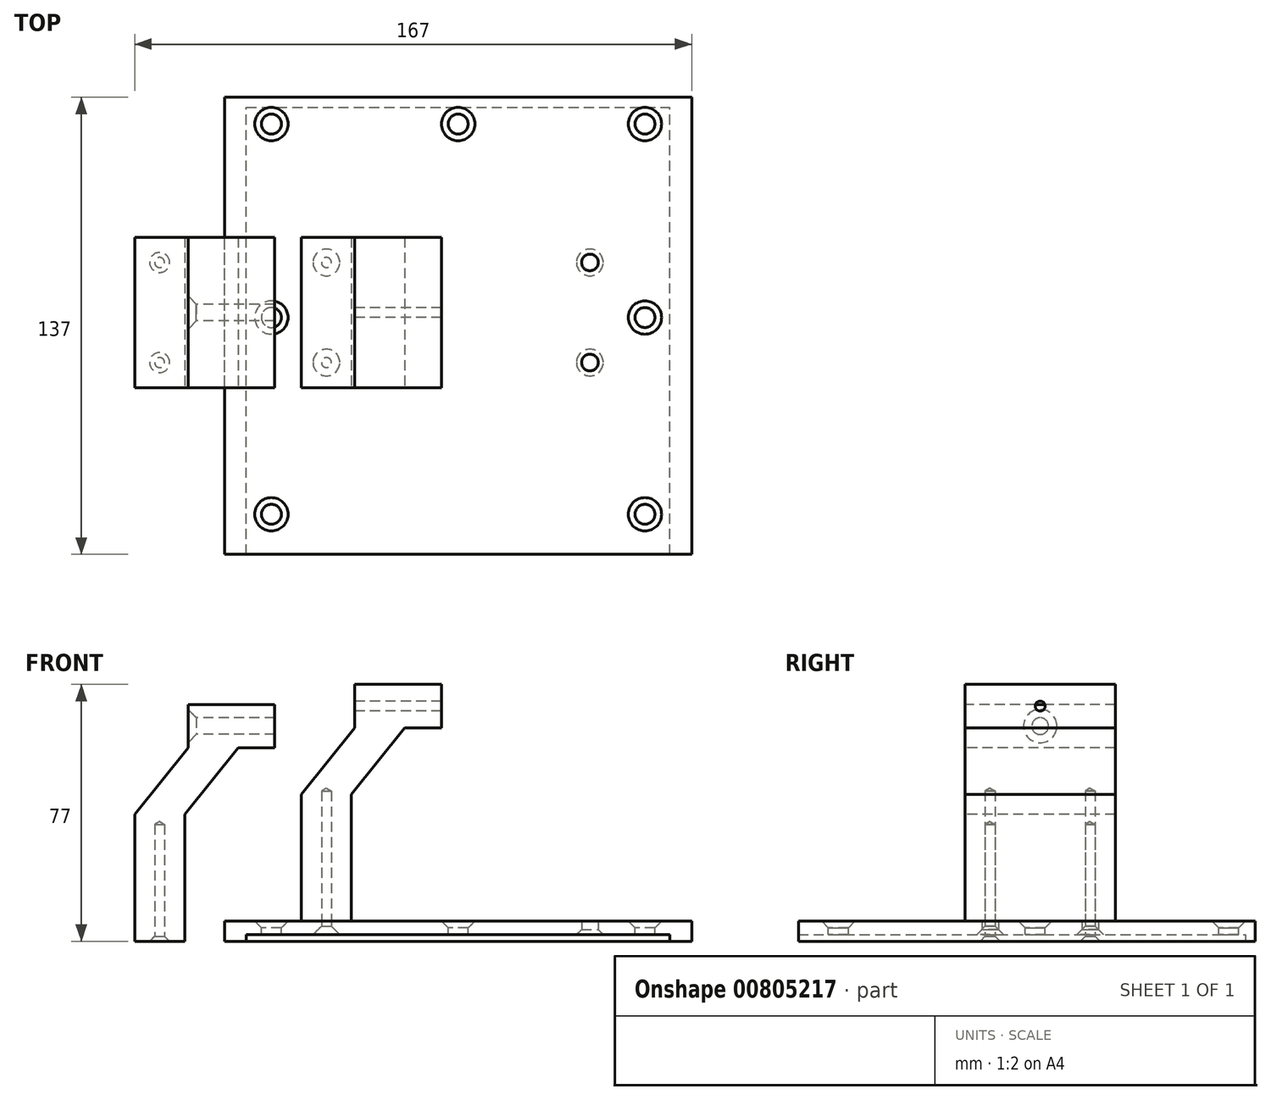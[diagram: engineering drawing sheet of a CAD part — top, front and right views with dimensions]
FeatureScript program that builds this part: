
annotation { "Feature Type Name" : "Feature", "Feature Type Description" : "" }
export const myFeature = defineFeature(function(context is Context, id is Id, definition is map)
    precondition{}
    {
        {
            var Q0;
            Q0=qCreatedBy(makeId("Top.planeOp"),FACE);
            var sketch = newSketch(context, id + "F0", { "sketchPlane" : qUnion([Q0])});
            skLineSegment(sketch, "E0.bottom", {"start": v(0, 0) * mm, "end": v(140, 0) * mm});
            skLineSegment(sketch, "E0.top", {"start": v(0, 137) * mm, "end": v(140, 137) * mm});
            skLineSegment(sketch, "E0.left", {"start": v(0, 0) * mm, "end": v(0, 137) * mm});
            skLineSegment(sketch, "E0.right", {"start": v(140, 0) * mm, "end": v(140, 137) * mm});
            skSolve(sketch);
        }
        {
            var Q0;
            Q0=makeQuery(id+"F0.imprint","IMPRINT",FACE,{"disambiguationData":[TD([[makeQuery(id+"F0.imprint","IMPRINT",EDGE,{"derivedFrom":sQuery(id+"F0.wireOp",EDGE,"E0.bottom")}),1.0]])]});
            extrude(context, id + "F1", {"entities" : qUnion([Q0]), "depth" : 6 * mm, "offsetDistance" : 25 * mm});
        }
        {
            var Q0;
            Q0=makeQuery(id+"F1.opExtrude","CAP_FACE",FACE,{"disambiguationData":[OSD([sQuery(id+"F0.wireOp",EDGE,"E0.bottom"),sQuery(id+"F0.wireOp",EDGE,"E0.top"),sQuery(id+"F0.wireOp",EDGE,"E0.left"),sQuery(id+"F0.wireOp",EDGE,"E0.right")])],"isStart":false});
            var sketch = newSketch(context, id + "F2", { "sketchPlane" : qUnion([Q0])});
            skLineSegment(sketch, "E1", {"start": v(70, 137) * mm, "end": v(70, 0) * mm, "construction": true});
            skLineSegment(sketch, "E2", {"start": v(0, 129) * mm, "end": v(140, 129) * mm, "construction": true});
            skLineSegment(sketch, "E3", {"start": v(0, 107) * mm, "end": v(140, 107) * mm, "construction": true});
            skPoint(sketch, "E4", {"position": v(14, 129) * mm});
            skPoint(sketch, "E5", {"position": v(70, 129) * mm});
            skPoint(sketch, "E6", {"position": v(126, 129) * mm});
            skPoint(sketch, "E7", {"position": v(18, 107) * mm});
            skPoint(sketch, "E8", {"position": v(122, 107) * mm});
            skLineSegment(sketch, "E9", {"start": v(0, 12) * mm, "end": v(140, 12) * mm, "construction": true});
            skLineSegment(sketch, "E10", {"start": v(0, 71) * mm, "end": v(140, 71) * mm, "construction": true});
            skLineSegment(sketch, "E11", {"start": v(14, 135.44) * mm, "end": v(14, 12) * mm, "construction": true});
            skLineSegment(sketch, "E12", {"start": v(126, 12) * mm, "end": v(126, 129) * mm, "construction": true});
            skPoint(sketch, "E13", {"position": v(14, 12) * mm});
            skPoint(sketch, "E14", {"position": v(126, 12) * mm});
            skPoint(sketch, "E15", {"position": v(126, 71) * mm});
            skPoint(sketch, "E16", {"position": v(14, 71) * mm});
            skSolve(sketch);
        }
        {
            var Q0;
            Q0=sQuery(id+"F2.wireOp",VERTEX,"E4");
            var Q1;
            Q1=sQuery(id+"F2.wireOp",VERTEX,"E5");
            var Q2;
            Q2=sQuery(id+"F2.wireOp",VERTEX,"E6");
            var Q3;
            Q3=sQuery(id+"F2.wireOp",VERTEX,"E16");
            var Q4;
            Q4=sQuery(id+"F2.wireOp",VERTEX,"E15");
            var Q5;
            Q5=sQuery(id+"F2.wireOp",VERTEX,"E14");
            var Q6;
            Q6=sQuery(id+"F2.wireOp",VERTEX,"E13");
            var Q7;
            Q7=makeQuery(id+"F1.opExtrude","SWEPT_BODY",BODY,{"disambiguationData":[OSD([sQuery(id+"F0.wireOp",EDGE,"E0.bottom"),sQuery(id+"F0.wireOp",EDGE,"E0.top"),sQuery(id+"F0.wireOp",EDGE,"E0.left"),sQuery(id+"F0.wireOp",EDGE,"E0.right")])]});
            hole(context, id + "F3", {"style" : HoleStyle.C_SINK, "endStyle" : HoleEndStyle.THROUGH, "holeDiameter" : 6 * mm, "cSinkDiameter" : 10 * mm, "cSinkAngle" : 90 * degree, "majorDiameter" : 5 * mm, "isTappedThrough" : true, "tappedDepth" : 12 * mm, "tapClearance" : 3, "startFromSketch" : true, "locations" : qUnion([Q0, Q1, Q2, Q3, Q4, Q5, Q6]), "scope" : qUnion([Q7])});
        }
        {
            var Q0;
            Q0=makeQuery(id+"FzE8ZDCXC4sYmEn_1.boolean.opBoolean","MERGE",FACE,{"derivedFrom":[makeQuery(id+"F1.opExtrude","SWEPT_FACE",FACE,{"disambiguationData":[OSD([sQuery(id+"F0.wireOp",EDGE,"E0.bottom")])]}),makeQuery(id+"FzE8ZDCXC4sYmEn_1.opExtrude","SWEPT_FACE",FACE,{"disambiguationData":[OSD([sQuery(id+"FCP8l3nhgKFZF62_1.wireOp",EDGE,"6PEErpOA-bjMb-Vwhj-6amR-bHppJGbZV4a9.bottom")])]}),makeQuery(id+"FzE8ZDCXC4sYmEn_1.opExtrude","SWEPT_FACE",FACE,{"disambiguationData":[OSD([sQuery(id+"FCP8l3nhgKFZF62_1.wireOp",EDGE,"gd5vmW88-UjtB-D9mt-sBeu-wjY4mzePWb4o.bottom")])]})]});
            var sketch = newSketch(context, id + "F4", { "sketchPlane" : qUnion([Q0])});
            skLineSegment(sketch, "E17", {"start": v(23, 44) * mm, "end": v(39, 64) * mm});
            skLineSegment(sketch, "E18", {"start": v(39, 64) * mm, "end": v(39, 77) * mm});
            skLineSegment(sketch, "E19", {"start": v(39, 77) * mm, "end": v(54, 77) * mm});
            skLineSegment(sketch, "E20", {"start": v(38, 44) * mm, "end": v(54, 64) * mm});
            skLineSegment(sketch, "E21", {"start": v(54, 64) * mm, "end": v(54, 77) * mm});
            skLineSegment(sketch, "E22", {"start": v(70, 6) * mm, "end": v(70, 104.41) * mm, "construction": true});
            skLineSegment(sketch, "E23", {"start": v(23, 44) * mm, "end": v(38, 44) * mm});
            skLineSegment(sketch, "E24", {"start": v(23, 44) * mm, "end": v(23, 6) * mm});
            skLineSegment(sketch, "E25", {"start": v(38, 44) * mm, "end": v(38, 6) * mm});
            skLineSegment(sketch, "E26", {"start": v(23, 6) * mm, "end": v(38, 6) * mm});
            skLineSegment(sketch, "E27", {"start": v(39, 64) * mm, "end": v(54, 64) * mm});
            skSolve(sketch);
        }
        {
            var Q0;
            Q0=makeQuery(id+"F4.imprint","IMPRINT",FACE,{"disambiguationData":[TD([[makeQuery(id+"F4.imprint","IMPRINT",EDGE,{"derivedFrom":sQuery(id+"F4.wireOp",EDGE,"E23")}),-1.0]])]});
            var Q1;
            Q1=makeQuery(id+"F4.imprint","IMPRINT",FACE,{"disambiguationData":[TD([[makeQuery(id+"F4.imprint","IMPRINT",EDGE,{"derivedFrom":sQuery(id+"F4.wireOp",EDGE,"E17")}),-1.0]])]});
            var Q2;
            Q2=makeQuery(id+"F4.imprint","IMPRINT",FACE,{"disambiguationData":[TD([[makeQuery(id+"F4.imprint","IMPRINT",EDGE,{"derivedFrom":sQuery(id+"F4.wireOp",EDGE,"E18")}),-1.0]])]});
            extrude(context, id + "F5", {"entities" : qUnion([Q0, Q1, Q2]), "oppositeDirection" : true, "depth" : 45 * mm, "offsetDistance" : 25 * mm});
        }
        {
            var Q0;
            Q0=makeQuery(id+"F5.opExtrude","SWEPT_FACE",FACE,{"disambiguationData":[OSD([sQuery(id+"F4.wireOp",EDGE,"E21")])]});
            extrude(context, id + "F6", {"entities" : qUnion([Q0]), "operationType" : NewBodyOperationType.ADD, "depth" : 11 * mm, "offsetDistance" : 25 * mm});
        }
        {
            var Q0;
            Q0=makeQuery(id+"F5.opExtrude","SWEPT_BODY",BODY,{"disambiguationData":[OSD([sQuery(id+"F4.wireOp",EDGE,"E17"),sQuery(id+"F4.wireOp",EDGE,"E18"),sQuery(id+"F4.wireOp",EDGE,"E19"),sQuery(id+"F4.wireOp",EDGE,"E20"),sQuery(id+"F4.wireOp",EDGE,"E21"),sQuery(id+"F4.wireOp",EDGE,"E24"),sQuery(id+"F4.wireOp",EDGE,"E25"),sQuery(id+"F4.wireOp",EDGE,"E26")])]});
            transform(context, id + "F7", {"entities" : qUnion([Q0]), "transformType" : TransformType.TRANSLATION_3D, "dx" : -50 * mm, "dy" : 50 * mm, "dz" : -6 * mm, "makeCopy" : true});
        }
        {
            var Q0;
            Q0=makeQuery(id+"F7.opPattern","COPY",FACE,{"derivedFrom":makeQuery(id+"F5.opExtrude","SWEPT_FACE",FACE,{"disambiguationData":[OSD([sQuery(id+"F4.wireOp",EDGE,"E18")])]}),"instanceName":"1"});
            var sketch = newSketch(context, id + "F8", { "sketchPlane" : qUnion([Q0])});
            skLineSegment(sketch, "E28", {"start": v(-95, 64.5) * mm, "end": v(-50, 64.5) * mm, "construction": true});
            skLineSegment(sketch, "E29", {"start": v(-72.5, 71) * mm, "end": v(-72.5, 58) * mm, "construction": true});
            skPoint(sketch, "E30", {"position": v(-72.5, 64.5) * mm});
            skSolve(sketch);
        }
        {
            var Q0;
            Q0=sQuery(id+"F8.wireOp",VERTEX,"E30");
            var Q1;
            Q1=makeQuery(id+"F7.opPattern","COPY",BODY,{"derivedFrom":makeQuery(id+"F5.opExtrude","SWEPT_BODY",BODY,{"disambiguationData":[OSD([sQuery(id+"F4.wireOp",EDGE,"E17"),sQuery(id+"F4.wireOp",EDGE,"E18"),sQuery(id+"F4.wireOp",EDGE,"E19"),sQuery(id+"F4.wireOp",EDGE,"E20"),sQuery(id+"F4.wireOp",EDGE,"E21"),sQuery(id+"F4.wireOp",EDGE,"E24"),sQuery(id+"F4.wireOp",EDGE,"E25"),sQuery(id+"F4.wireOp",EDGE,"E26")])]}),"instanceName":"1"});
            hole(context, id + "F9", {"style" : HoleStyle.C_SINK, "endStyle" : HoleEndStyle.BLIND, "holeDiameter" : 5 * mm, "cSinkDiameter" : 10 * mm, "cSinkAngle" : 90 * degree, "majorDiameter" : 5 * mm, "holeDepth" : 35 * mm, "isTappedThrough" : true, "tappedDepth" : 12 * mm, "tapClearance" : 3, "startFromSketch" : true, "locations" : qUnion([Q0]), "scope" : qUnion([Q1])});
        }
        {
            var Q0;
            Q0=makeQuery(id+"F7.opPattern","COPY",FACE,{"derivedFrom":makeQuery(id+"F5.opExtrude","SWEPT_FACE",FACE,{"disambiguationData":[OSD([sQuery(id+"F4.wireOp",EDGE,"E26")])]}),"instanceName":"1"});
            var sketch = newSketch(context, id + "F10", { "sketchPlane" : qUnion([Q0])});
            skLineSegment(sketch, "E31", {"start": v(-19.5, -50) * mm, "end": v(-19.5, -95) * mm, "construction": true});
            skLineSegment(sketch, "E32", {"start": v(109.5, 0) * mm, "end": v(109.5, -30) * mm, "construction": true});
            skPoint(sketch, "E33", {"position": v(-19.5, -57.5) * mm});
            skPoint(sketch, "E34", {"position": v(-19.5, -87.5) * mm});
            skLineSegment(sketch, "E35", {"start": v(-19.5, -57.5) * mm, "end": v(109.5, -57.5) * mm, "construction": true});
            skLineSegment(sketch, "E36", {"start": v(-19.5, -87.5) * mm, "end": v(109.5, -87.5) * mm, "construction": true});
            skPoint(sketch, "E37", {"position": v(109.5, -57.5) * mm});
            skPoint(sketch, "E38", {"position": v(109.5, -87.5) * mm});
            skLineSegment(sketch, "E39", {"start": v(30.5, -57.5) * mm, "end": v(30.5, -87.5) * mm, "construction": true});
            skPoint(sketch, "E40", {"position": v(30.5, -87.5) * mm});
            skPoint(sketch, "E41", {"position": v(30.5, -57.5) * mm});
            skSolve(sketch);
        }
        {
            var Q0;
            Q0=sQuery(id+"F10.wireOp",VERTEX,"E33");
            var Q1;
            Q1=makeQuery(id+"F7.opPattern","COPY",BODY,{"derivedFrom":makeQuery(id+"F5.opExtrude","SWEPT_BODY",BODY,{"disambiguationData":[OSD([sQuery(id+"F4.wireOp",EDGE,"E17"),sQuery(id+"F4.wireOp",EDGE,"E18"),sQuery(id+"F4.wireOp",EDGE,"E19"),sQuery(id+"F4.wireOp",EDGE,"E20"),sQuery(id+"F4.wireOp",EDGE,"E21"),sQuery(id+"F4.wireOp",EDGE,"E24"),sQuery(id+"F4.wireOp",EDGE,"E25"),sQuery(id+"F4.wireOp",EDGE,"E26")])]}),"instanceName":"1"});
            hole(context, id + "F11", {"style" : HoleStyle.C_SINK, "endStyle" : HoleEndStyle.BLIND, "holeDiameter" : 3 * mm, "cSinkDiameter" : 6 * mm, "cSinkAngle" : 90 * degree, "majorDiameter" : 5 * mm, "holeDepth" : 35 * mm, "isTappedThrough" : true, "tappedDepth" : 12 * mm, "tapClearance" : 3, "startFromSketch" : true, "locations" : qUnion([Q0]), "scope" : qUnion([Q1])});
        }
        {
            var Q0;
            Q0=sQuery(id+"F10.wireOp",VERTEX,"E34");
            var Q1;
            Q1=makeQuery(id+"F7.opPattern","COPY",BODY,{"derivedFrom":makeQuery(id+"F5.opExtrude","SWEPT_BODY",BODY,{"disambiguationData":[OSD([sQuery(id+"F4.wireOp",EDGE,"E17"),sQuery(id+"F4.wireOp",EDGE,"E18"),sQuery(id+"F4.wireOp",EDGE,"E19"),sQuery(id+"F4.wireOp",EDGE,"E20"),sQuery(id+"F4.wireOp",EDGE,"E21"),sQuery(id+"F4.wireOp",EDGE,"E24"),sQuery(id+"F4.wireOp",EDGE,"E25"),sQuery(id+"F4.wireOp",EDGE,"E26")])]}),"instanceName":"1"});
            hole(context, id + "F12", {"style" : HoleStyle.C_SINK, "endStyle" : HoleEndStyle.BLIND, "holeDiameter" : 3 * mm, "cSinkDiameter" : 6 * mm, "cSinkAngle" : 90 * degree, "majorDiameter" : 5 * mm, "holeDepth" : 35 * mm, "isTappedThrough" : true, "tappedDepth" : 12 * mm, "tapClearance" : 3, "startFromSketch" : true, "locations" : qUnion([Q0]), "scope" : qUnion([Q1])});
        }
        {
            var Q0;
            Q0=makeQuery(id+"F5.opExtrude","SWEPT_FACE",FACE,{"disambiguationData":[OSD([sQuery(id+"F4.wireOp",EDGE,"E18")])]});
            var sketch = newSketch(context, id + "F13", { "sketchPlane" : qUnion([Q0])});
            skLineSegment(sketch, "E42", {"start": v(-22.5, 77) * mm, "end": v(-22.5, 64) * mm, "construction": true});
            skLineSegment(sketch, "E43", {"start": v(0, 70.5) * mm, "end": v(-45, 70.5) * mm, "construction": true});
            skPoint(sketch, "E44", {"position": v(-22.5, 70.5) * mm});
            skSolve(sketch);
        }
        {
            var Q0;
            Q0=sQuery(id+"F13.wireOp",VERTEX,"E44");
            var Q1;
            Q1=makeQuery(id+"F5.opExtrude","SWEPT_BODY",BODY,{"disambiguationData":[OSD([sQuery(id+"F4.wireOp",EDGE,"E17"),sQuery(id+"F4.wireOp",EDGE,"E18"),sQuery(id+"F4.wireOp",EDGE,"E19"),sQuery(id+"F4.wireOp",EDGE,"E20"),sQuery(id+"F4.wireOp",EDGE,"E21"),sQuery(id+"F4.wireOp",EDGE,"E24"),sQuery(id+"F4.wireOp",EDGE,"E25"),sQuery(id+"F4.wireOp",EDGE,"E26")])]});
            hole(context, id + "F14", {"style" : HoleStyle.SIMPLE, "endStyle" : HoleEndStyle.BLIND, "holeDiameter" : 3 * mm, "majorDiameter" : 5 * mm, "holeDepth" : 35 * mm, "isTappedThrough" : true, "tappedDepth" : 12 * mm, "tapClearance" : 3, "startFromSketch" : true, "locations" : qUnion([Q0]), "scope" : qUnion([Q1])});
        }
        {
            var Q0;
            Q0=makeQuery(id+"F5.opExtrude","SWEPT_BODY",BODY,{"disambiguationData":[OSD([sQuery(id+"F4.wireOp",EDGE,"E17"),sQuery(id+"F4.wireOp",EDGE,"E18"),sQuery(id+"F4.wireOp",EDGE,"E19"),sQuery(id+"F4.wireOp",EDGE,"E20"),sQuery(id+"F4.wireOp",EDGE,"E21"),sQuery(id+"F4.wireOp",EDGE,"E24"),sQuery(id+"F4.wireOp",EDGE,"E25"),sQuery(id+"F4.wireOp",EDGE,"E26")])]});
            transform(context, id + "F15", {"entities" : qUnion([Q0]), "transformType" : TransformType.TRANSLATION_3D, "dx" : 0 * mm, "dy" : 50 * mm, "dz" : 0 * mm, "makeCopy" : false});
        }
        {
            var Q0;
            Q0=makeQuery(id+"F0.imprint","IMPRINT",FACE,{"disambiguationData":[TD([[makeQuery(id+"F0.imprint","IMPRINT",EDGE,{"derivedFrom":sQuery(id+"F0.wireOp",EDGE,"E0.bottom")}),1.0]])]});
            var sketch = newSketch(context, id + "F16", { "sketchPlane" : qUnion([Q0])});
            skLineSegment(sketch, "E45.bottom", {"start": v(6.5, -2) * mm, "end": v(133.5, -2) * mm});
            skLineSegment(sketch, "E45.top", {"start": v(6.5, 134) * mm, "end": v(133.5, 134) * mm});
            skLineSegment(sketch, "E45.left", {"start": v(6.5, -2) * mm, "end": v(6.5, 134) * mm});
            skLineSegment(sketch, "E45.right", {"start": v(133.5, -2) * mm, "end": v(133.5, 134) * mm});
            skPoint(sketch, "E45.middle", {"position": v(70, 66) * mm});
            skSolve(sketch);
        }
        {
            var Q0;
            Q0 = qSketchRegion(id + "F16", true);
            extrude(context, id + "F17", {"entities" : qUnion([Q0]), "operationType" : NewBodyOperationType.REMOVE, "depth" : 2 * mm, "offsetDistance" : 25 * mm});
        }
        {
            var Q0;
            Q0=sQuery(id+"F10.wireOp",VERTEX,"E37");
            var Q1;
            Q1=sQuery(id+"F10.wireOp",VERTEX,"E38");
            var Q2;
            Q2=makeQuery(id+"F1.opExtrude","SWEPT_BODY",BODY,{"disambiguationData":[OSD([sQuery(id+"F0.wireOp",EDGE,"E0.bottom"),sQuery(id+"F0.wireOp",EDGE,"E0.top"),sQuery(id+"F0.wireOp",EDGE,"E0.left"),sQuery(id+"F0.wireOp",EDGE,"E0.right")])]});
            hole(context, id + "F18", {"style" : HoleStyle.C_SINK, "endStyle" : HoleEndStyle.BLIND, "holeDiameter" : 5 * mm, "cSinkDiameter" : 12 * mm, "cSinkAngle" : 90 * degree, "majorDiameter" : 5 * mm, "holeDepth" : 11 * mm, "isTappedThrough" : true, "tappedDepth" : 12 * mm, "tapClearance" : 3, "startFromSketch" : true, "locations" : qUnion([Q0, Q1]), "scope" : qUnion([Q2])});
        }
        {
            var Q0;
            Q0=sQuery(id+"F10.wireOp",VERTEX,"E41");
            var Q1;
            Q1=sQuery(id+"F10.wireOp",VERTEX,"E40");
            var Q2;
            Q2=makeQuery(id+"F1.opExtrude","SWEPT_BODY",BODY,{"disambiguationData":[OSD([sQuery(id+"F0.wireOp",EDGE,"E0.bottom"),sQuery(id+"F0.wireOp",EDGE,"E0.top"),sQuery(id+"F0.wireOp",EDGE,"E0.left"),sQuery(id+"F0.wireOp",EDGE,"E0.right")])]});
            var Q3;
            Q3=makeQuery(id+"F5.opExtrude","SWEPT_BODY",BODY,{"disambiguationData":[OSD([sQuery(id+"F4.wireOp",EDGE,"E17"),sQuery(id+"F4.wireOp",EDGE,"E18"),sQuery(id+"F4.wireOp",EDGE,"E19"),sQuery(id+"F4.wireOp",EDGE,"E20"),sQuery(id+"F4.wireOp",EDGE,"E21"),sQuery(id+"F4.wireOp",EDGE,"E24"),sQuery(id+"F4.wireOp",EDGE,"E25"),sQuery(id+"F4.wireOp",EDGE,"E26")])]});
            hole(context, id + "F19", {"style" : HoleStyle.C_SINK, "endStyle" : HoleEndStyle.BLIND, "holeDiameter" : 3 * mm, "cSinkDiameter" : 12 * mm, "cSinkAngle" : 90 * degree, "majorDiameter" : 5 * mm, "holeDepth" : 45 * mm, "isTappedThrough" : true, "tappedDepth" : 12 * mm, "tapClearance" : 3, "startFromSketch" : true, "locations" : qUnion([Q0, Q1]), "scope" : qUnion([Q2, Q3])});
        }
    });
